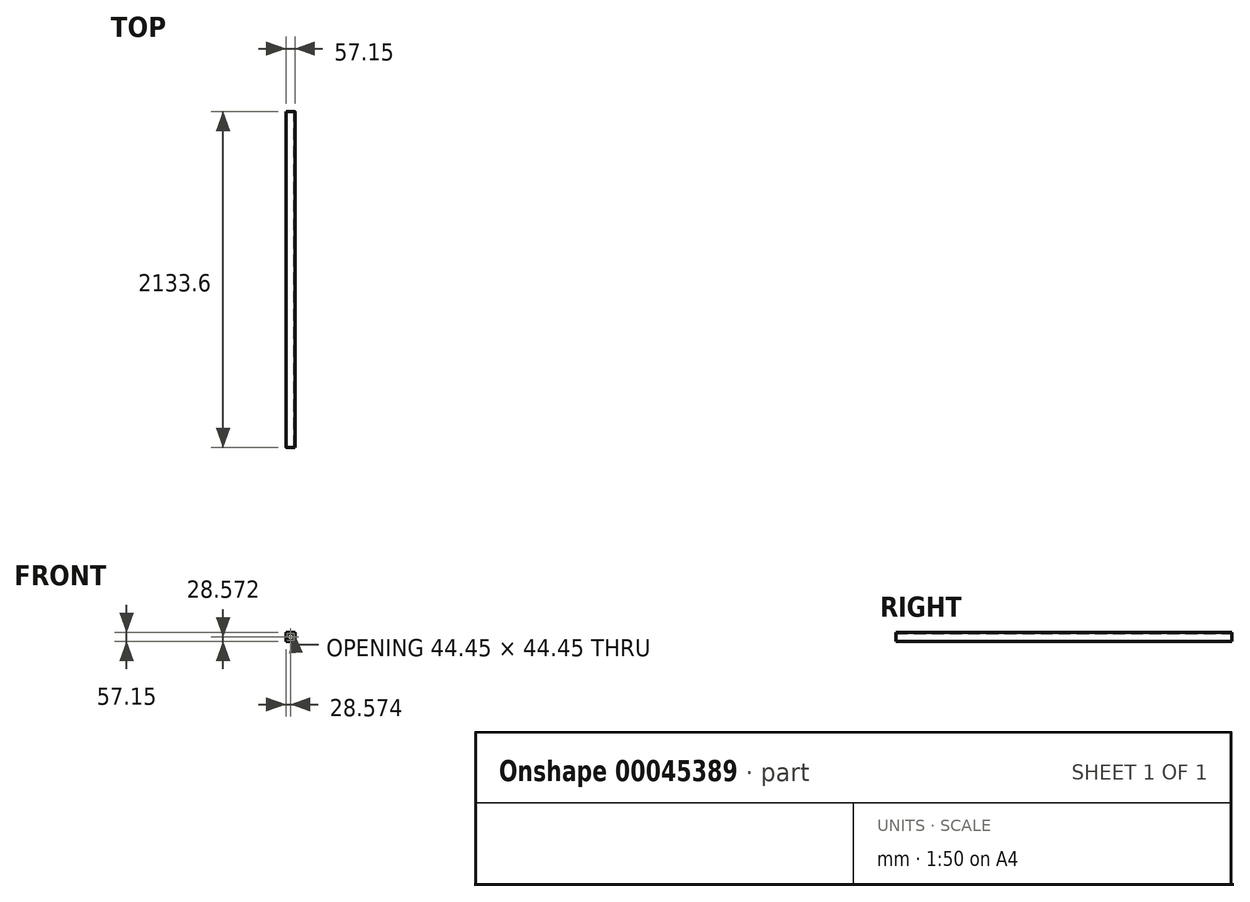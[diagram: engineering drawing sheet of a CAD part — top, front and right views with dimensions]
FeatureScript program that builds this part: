
annotation { "Feature Type Name" : "Feature", "Feature Type Description" : "" }
export const myFeature = defineFeature(function(context is Context, id is Id, definition is map)
    precondition{}
    {
        {
            var Q0;
            Q0=qCreatedBy(makeId("Front.planeOp"),FACE);
            var sketch = newSketch(context, id + "F0", { "sketchPlane" : qUnion([Q0])});
            skLineSegment(sketch, "E0.bottom", {"start": v(-27.58, 35.03) * mm, "end": v(24.49, 35.03) * mm});
            skLineSegment(sketch, "E0.top", {"start": v(-27.58, -22.12) * mm, "end": v(24.49, -22.12) * mm});
            skLineSegment(sketch, "E0.left", {"start": v(-30.12, 32.49) * mm, "end": v(-30.12, -19.58) * mm});
            skLineSegment(sketch, "E0.right", {"start": v(27.03, 32.49) * mm, "end": v(27.03, -19.58) * mm});
            skLineSegment(sketch, "E1.bottom", {"start": v(-21.23, 28.68) * mm, "end": v(20.68, 28.68) * mm});
            skLineSegment(sketch, "E1.top", {"start": v(-21.23, -15.77) * mm, "end": v(18.14, -15.77) * mm});
            skLineSegment(sketch, "E1.left", {"start": v(-23.77, 26.14) * mm, "end": v(-23.77, -13.23) * mm});
            skLineSegment(sketch, "E1.right", {"start": v(20.68, 28.68) * mm, "end": v(20.68, -13.23) * mm});
            skPoint(sketch, "E2.visualSharp", {"position": v(-30.12, 35.03) * mm});
            skArc(sketch, "E2.filletArc", {"start": v(-27.58, 35.03) * mm, "mid": v(-29.38, 34.28) * mm, "end": v(-30.12, 32.49) * mm});
            skPoint(sketch, "E3.visualSharp", {"position": v(-23.77, 28.68) * mm});
            skArc(sketch, "E3.filletArc", {"start": v(-21.23, 28.68) * mm, "mid": v(-23.03, 27.93) * mm, "end": v(-23.77, 26.14) * mm});
            skPoint(sketch, "E4.visualSharp", {"position": v(-30.12, -22.12) * mm});
            skArc(sketch, "E4.filletArc", {"start": v(-30.12, -19.58) * mm, "mid": v(-29.38, -21.38) * mm, "end": v(-27.58, -22.12) * mm});
            skPoint(sketch, "E5.visualSharp", {"position": v(-23.77, -15.77) * mm});
            skArc(sketch, "E5.filletArc", {"start": v(-23.77, -13.23) * mm, "mid": v(-23.03, -15.03) * mm, "end": v(-21.23, -15.77) * mm});
            skPoint(sketch, "E6.visualSharp", {"position": v(20.68, -15.77) * mm});
            skArc(sketch, "E6.filletArc", {"start": v(18.14, -15.77) * mm, "mid": v(19.93, -15.03) * mm, "end": v(20.68, -13.23) * mm});
            skPoint(sketch, "E7.visualSharp", {"position": v(27.03, -22.12) * mm});
            skArc(sketch, "E7.filletArc", {"start": v(24.49, -22.12) * mm, "mid": v(26.28, -21.38) * mm, "end": v(27.03, -19.58) * mm});
            skPoint(sketch, "E8.visualSharp", {"position": v(27.03, 35.03) * mm});
            skArc(sketch, "E8.filletArc", {"start": v(27.03, 32.49) * mm, "mid": v(26.28, 34.28) * mm, "end": v(24.49, 35.03) * mm});
            skSolve(sketch);
        }
        {
            var Q0;
            Q0=makeQuery(id+"F0.imprint","IMPRINT",FACE,{"disambiguationData":[TD([[makeQuery(id+"F0.imprint","IMPRINT",EDGE,{"derivedFrom":sQuery(id+"F0.wireOp",EDGE,"E0.bottom")}),-1.0]])]});
            extrude(context, id + "F1", {"entities" : qUnion([Q0]), "depth" : 2133.6 * mm});
        }
    });
